# Revit family: 5-SHEET-CADS-19-1-4-X-4-4-REVIT_Versatex-Generic-Model-1-4in-x-48in-SHEET
name_source: partatom
category: Generic Models
units: mm (PartAtom-declared; Revit-internal decimal feet)

## family parameters
Can host rebar = No
Cut with Voids When Loaded = No
Host = Face
Maintain Annotation Orientation = No
Part Type = Normal
Room Calculation Point = No
Round Connector Dimension = Use Diameter
Shared = No

## types (1)
- 5-SHEET-CADS-19-1-4-X-4-4-REVIT_Versatex-Generic-Model-1-4in-x-48in-SHEET
    Default Elevation = 4' - 0"
    Literature = https://versatex.com
    Manufacturer = Versatex
    Manufacturer Fax = 724-857-1171
    Manufacturer Website = https://versatex.com
    Material = Versatex PVC - Smooth
    Message Manufacturer = https://versatex.com
    Sales Information = https://versatex.com
    Specification = https://www.arcat.com
    URL = https://versatex.com
    Warranty = https://versatex.com

## geometry (parser evidence)
native form markers: Sweep x3
no freeform markers — native parametric forms only
